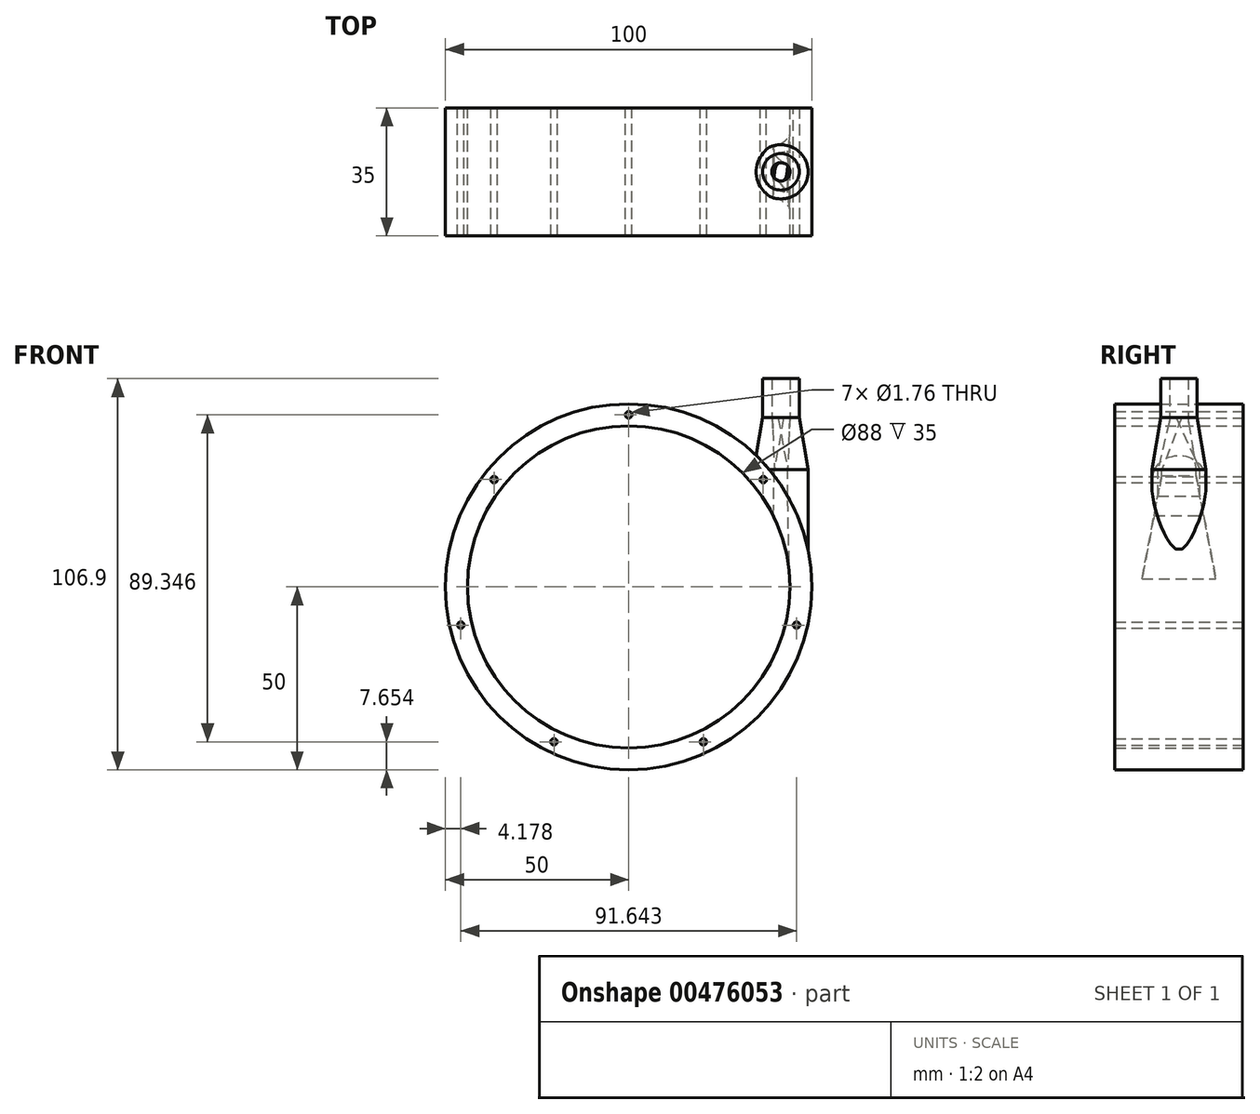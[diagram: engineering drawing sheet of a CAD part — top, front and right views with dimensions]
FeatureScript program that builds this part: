
annotation { "Feature Type Name" : "Feature", "Feature Type Description" : "" }
export const myFeature = defineFeature(function(context is Context, id is Id, definition is map)
    precondition{}
    {
        {
            var Q0;
            Q0=qCreatedBy(makeId("Front.planeOp"),FACE);
            var sketch = newSketch(context, id + "F0", { "sketchPlane" : qUnion([Q0])});
            skCircle(sketch, "E0", {"center": v(0, 0) * mm, "radius": 50 * mm});
            skCircle(sketch, "E1", {"center": v(0, 0) * mm, "radius": 44 * mm});
            skCircle(sketch, "E2", {"center": v(0, 47) * mm, "radius": 0.88 * mm});
            skCircle(sketch, "E3.1.0", {"center": v(-36.75, 29.3) * mm, "radius": 0.88 * mm});
            skCircle(sketch, "E3.2.0", {"center": v(-45.82, -10.46) * mm, "radius": 0.88 * mm});
            skCircle(sketch, "E3.3.0", {"center": v(-20.4, -42.35) * mm, "radius": 0.88 * mm});
            skCircle(sketch, "E3.4.0", {"center": v(20.4, -42.35) * mm, "radius": 0.88 * mm});
            skCircle(sketch, "E3.5.0", {"center": v(45.82, -10.46) * mm, "radius": 0.88 * mm});
            skCircle(sketch, "E3.6.0", {"center": v(36.75, 29.3) * mm, "radius": 0.88 * mm});
            skSolve(sketch);
        }
        {
            var Q0;
            Q0=makeQuery(id+"F0.imprint","IMPRINT",FACE,{"disambiguationData":[TD([[makeQuery(id+"F0.imprint","IMPRINT",EDGE,{"derivedFrom":sQuery(id+"F0.wireOp",EDGE,"E0")}),1.0]])]});
            extrude(context, id + "F1", {"entities" : qUnion([Q0]), "depth" : 35 * mm});
        }
        {
            var Q0;
            Q0=qCreatedBy(makeId("Top.planeOp"),FACE);
            var sketch = newSketch(context, id + "F2", { "sketchPlane" : qUnion([Q0])});
            skLineSegment(sketch, "E4", {"start": v(44, 0) * mm, "end": v(44, -35) * mm});
            skLineSegment(sketch, "E5", {"start": v(-44, -35) * mm, "end": v(-44, 0) * mm});
            skLineSegment(sketch, "E6.bottom", {"start": v(44, -7) * mm, "end": v(39, -7) * mm});
            skLineSegment(sketch, "E6.top", {"start": v(44, -28) * mm, "end": v(39, -28) * mm});
            skLineSegment(sketch, "E6.left", {"start": v(44, -7) * mm, "end": v(44, -28) * mm});
            skLineSegment(sketch, "E6.right", {"start": v(39, -7) * mm, "end": v(39, -28) * mm});
            skLineSegment(sketch, "E7", {"start": v(50, 0) * mm, "end": v(50, -35) * mm});
            skLineSegment(sketch, "E8", {"start": v(-50, -35) * mm, "end": v(-50, 0) * mm});
            skLineSegment(sketch, "E9.0", {"start": v(50, -35) * mm, "end": v(-50, -35) * mm});
            skSolve(sketch);
        }
        {
            var Q0;
            Q0=qCreatedBy(makeId("Top.planeOp"),FACE);
            cPlane(context, id + "F3", {"entities" : qUnion([Q0]), "cplaneType" : CPlaneType.OFFSET, "offset" : 32 * mm, "width" : 150 * mm, "height" : 150 * mm});
        }
        {
            var Q0;
            Q0=qCreatedBy(id+"F3.planeOp",FACE);
            var sketch = newSketch(context, id + "F4", { "sketchPlane" : qUnion([Q0])});
            skLineSegment(sketch, "E10.0", {"start": v(44, -7) * mm, "end": v(39, -7) * mm});
            skLineSegment(sketch, "E11.0", {"start": v(44, -7) * mm, "end": v(44, -28) * mm});
            skLineSegment(sketch, "E12.0", {"start": v(39, -7) * mm, "end": v(39, -28) * mm});
            skPoint(sketch, "E13.0", {"position": v(41.5, -28) * mm});
            skLineSegment(sketch, "E14.0", {"start": v(44, -28) * mm, "end": v(39, -28) * mm});
            skLineSegment(sketch, "E15", {"start": v(41.5, -7) * mm, "end": v(41.5, -17.5) * mm});
            skPoint(sketch, "E15.endSnap0", {"position": v(44, -17.5) * mm});
            skLineSegment(sketch, "E16.bottom", {"start": v(43.22, -13.13) * mm, "end": v(39.78, -13.13) * mm});
            skLineSegment(sketch, "E16.top", {"start": v(43.22, -21.87) * mm, "end": v(39.78, -21.87) * mm});
            skLineSegment(sketch, "E16.left", {"start": v(43.22, -13.13) * mm, "end": v(43.22, -21.87) * mm});
            skLineSegment(sketch, "E16.right", {"start": v(39.78, -13.13) * mm, "end": v(39.78, -21.87) * mm});
            skPoint(sketch, "E16.middle", {"position": v(41.5, -17.5) * mm});
            skSolve(sketch);
        }
        {
            var Q1;
            Q1=makeQuery(id+"F2.imprint","IMPRINT",FACE,{"disambiguationData":[TD([[makeQuery(id+"F2.imprint","IMPRINT",EDGE,{"derivedFrom":sQuery(id+"F2.wireOp",EDGE,"E6.bottom")}),1.0]])]});
            var Q2;
            Q2=makeQuery(id+"F4.imprint","IMPRINT",FACE,{"disambiguationData":[TD([[makeQuery(id+"F4.imprint","IMPRINT",EDGE,{"derivedFrom":sQuery(id+"F4.wireOp",EDGE,"E16.top")}),-1.0]])]});
            loft(context, id + "F5", {"operationType" : NewBodyOperationType.REMOVE, "sheetProfilesArray" : [{ "sheetProfileEntities" : qUnion([Q1]) }, { "sheetProfileEntities" : qUnion([Q2]) }]});
        }
        {
            var Q0;
            Q0=qCreatedBy(id+"F3.planeOp",FACE);
            cPlane(context, id + "F6", {"entities" : qUnion([Q0]), "cplaneType" : CPlaneType.OFFSET, "offset" : 14.2 * mm, "width" : 150 * mm, "height" : 150 * mm});
        }
        {
            var Q0;
            Q0=qCreatedBy(id+"F3.planeOp",FACE);
            var sketch = newSketch(context, id + "F7", { "sketchPlane" : qUnion([Q0])});
            skLineSegment(sketch, "E17.0", {"start": v(43.4, -11.76) * mm, "end": v(43.4, -23.24) * mm});
            skPoint(sketch, "E18.0", {"position": v(41.66, -12.3) * mm});
            skEllipticalArc(sketch, "E19.0", {});
            skLineSegment(sketch, "E20.0", {"start": v(39.74, -22.19) * mm, "end": v(39.74, -12.81) * mm});
            skPoint(sketch, "E21.0", {"position": v(41.66, -22.7) * mm});
            skEllipticalArc(sketch, "E22.0", {});
            skLineSegment(sketch, "E23", {"start": v(43.4, -17.5) * mm, "end": v(39.74, -17.5) * mm, "construction": true});
            skCircle(sketch, "E24", {"center": v(41.57, -17.5) * mm, "radius": 7.4 * mm});
            skLineSegment(sketch, "E25", {"start": v(38.46, -24.23) * mm, "end": v(38.46, -10.77) * mm});
            const initialGuessF7  = {"E19.0": [0, -0.007, -1, 0, 0.05, 0.009581630339380354, 2.489497642671397, 2.6217003761671647], "E22.0": [0, -0.028, -1, 0, 0.05, 0.009581630339380356, 3.661484931012421, 3.7936876645081887]};
            skSetInitialGuess(sketch, initialGuessF7);
            skSolve(sketch);
        }
        {
            var Q0;
            Q0=makeQuery(id+"F7.imprint","IMPRINT",FACE,{"disambiguationData":[TD([[makeQuery(id+"F7.imprint","IMPRINT",EDGE,{"derivedFrom":sQuery(id+"F7.wireOp",EDGE,"E17.0")}),1.0]])]});
            var Q1;
            Q1=makeQuery(id+"F1.opExtrude","SWEPT_BODY",BODY,{"disambiguationData":[OSD([sQuery(id+"F0.wireOp",EDGE,"E0"),sQuery(id+"F0.wireOp",EDGE,"E1"),sQuery(id+"F0.wireOp",EDGE,"E2"),sQuery(id+"F0.wireOp",EDGE,"E3.1.0"),sQuery(id+"F0.wireOp",EDGE,"E3.2.0"),sQuery(id+"F0.wireOp",EDGE,"E3.3.0"),sQuery(id+"F0.wireOp",EDGE,"E3.4.0"),sQuery(id+"F0.wireOp",EDGE,"E3.5.0"),sQuery(id+"F0.wireOp",EDGE,"E3.6.0")])]});
            extrude(context, id + "F8", {"entities" : qUnion([Q0]), "operationType" : NewBodyOperationType.ADD, "endBound" : BoundingType.UP_TO_BODY, "oppositeDirection" : true, "endBoundEntityBody" : qUnion([Q1]), "depth" : 25 * mm});
        }
        {
            var Q0;
            Q0=makeQuery(id+"F8.opExtrude","SWEPT_FACE",FACE,{"disambiguationData":[OSD([sQuery(id+"F7.wireOp",EDGE,"E25")])]});
            var Q1;
            Q1=makeQuery(id+"F1.opExtrude","SWEPT_BODY",BODY,{"disambiguationData":[OSD([sQuery(id+"F0.wireOp",EDGE,"E0"),sQuery(id+"F0.wireOp",EDGE,"E1"),sQuery(id+"F0.wireOp",EDGE,"E2"),sQuery(id+"F0.wireOp",EDGE,"E3.1.0"),sQuery(id+"F0.wireOp",EDGE,"E3.2.0"),sQuery(id+"F0.wireOp",EDGE,"E3.3.0"),sQuery(id+"F0.wireOp",EDGE,"E3.4.0"),sQuery(id+"F0.wireOp",EDGE,"E3.5.0"),sQuery(id+"F0.wireOp",EDGE,"E3.6.0")])]});
            extrude(context, id + "F9", {"entities" : qUnion([Q0]), "operationType" : NewBodyOperationType.ADD, "endBound" : BoundingType.UP_TO_BODY, "endBoundEntityBody" : qUnion([Q1]), "depth" : 25 * mm});
        }
        {
            var Q0;
            Q0=qCreatedBy(id+"F6.planeOp",FACE);
            var sketch = newSketch(context, id + "F10", { "sketchPlane" : qUnion([Q0])});
            skArc(sketch, "E26.0", {"start": v(38.46, -24.23) * mm, "mid": v(48.98, -17.5) * mm, "end": v(38.46, -10.77) * mm});
            skCircle(sketch, "E27", {"center": v(41.57, -17.5) * mm, "radius": 5 * mm});
            skSolve(sketch);
        }
        {
            var Q0;
            Q0=qCreatedBy(id+"F3.planeOp",FACE);
            var sketch = newSketch(context, id + "F11", { "sketchPlane" : qUnion([Q0])});
            skCircle(sketch, "E28.0", {"center": v(41.57, -17.5) * mm, "radius": 7.4 * mm});
            skSolve(sketch);
        }
        {
            var Q1;
            Q1=makeQuery(id+"F11.imprint","IMPRINT",FACE,{"disambiguationData":[TD([[makeQuery(id+"F11.imprint","IMPRINT",EDGE,{"derivedFrom":sQuery(id+"F11.wireOp",EDGE,"E28.0")}),1.0]])]});
            var Q2;
            Q2=makeQuery(id+"F10.imprint","IMPRINT",FACE,{"disambiguationData":[TD([[makeQuery(id+"F10.imprint","IMPRINT",EDGE,{"derivedFrom":sQuery(id+"F10.wireOp",EDGE,"E27")}),1.0]])]});
            loft(context, id + "F12", {"operationType" : NewBodyOperationType.ADD, "sheetProfilesArray" : [{ "sheetProfileEntities" : qUnion([Q1]) }, { "sheetProfileEntities" : qUnion([Q2]) }]});
        }
        {
            var Q0;
            Q0=makeQuery(id+"F12.opLoft","CAP_FACE",FACE,{"disambiguationData":[OSD([makeQuery(id+"F10.imprint","IMPRINT",FACE,{"disambiguationData":[TD([[makeQuery(id+"F10.imprint","IMPRINT",EDGE,{"derivedFrom":sQuery(id+"F10.wireOp",EDGE,"E27")}),1.0]])]})])],"isStart":true});
            var sketch = newSketch(context, id + "F13", { "sketchPlane" : qUnion([Q0])});
            skCircle(sketch, "E29.0.0", {"center": v(41.57, -17.5) * mm, "radius": 5 * mm});
            skCircle(sketch, "E30", {"center": v(41.57, -17.5) * mm, "radius": 2.5 * mm});
            skSolve(sketch);
        }
        {
            var Q1;
            Q1=makeQuery(id+"F13.imprint","IMPRINT",FACE,{"disambiguationData":[TD([[makeQuery(id+"F13.imprint","IMPRINT",EDGE,{"derivedFrom":sQuery(id+"F13.wireOp",EDGE,"E30")}),1.0]])]});
            var Q2;
            Q2=makeQuery(id+"F7.imprint","IMPRINT",FACE,{"disambiguationData":[TD([[makeQuery(id+"F7.imprint","IMPRINT",EDGE,{"derivedFrom":sQuery(id+"F7.wireOp",EDGE,"E17.0")}),-1.0]])]});
            loft(context, id + "F14", {"operationType" : NewBodyOperationType.REMOVE, "sheetProfilesArray" : [{ "sheetProfileEntities" : qUnion([Q1]) }, { "sheetProfileEntities" : qUnion([Q2]) }]});
        }
        {
            var Q0;
            Q0=makeQuery(id+"F12.opLoft","CAP_FACE",FACE,{"disambiguationData":[OSD([makeQuery(id+"F10.imprint","IMPRINT",FACE,{"disambiguationData":[TD([[makeQuery(id+"F10.imprint","IMPRINT",EDGE,{"derivedFrom":sQuery(id+"F10.wireOp",EDGE,"E27")}),1.0]])]})])],"isStart":true});
            extrude(context, id + "F15", {"entities" : qUnion([Q0]), "operationType" : NewBodyOperationType.ADD, "depth" : 10.7 * mm});
        }
    });
